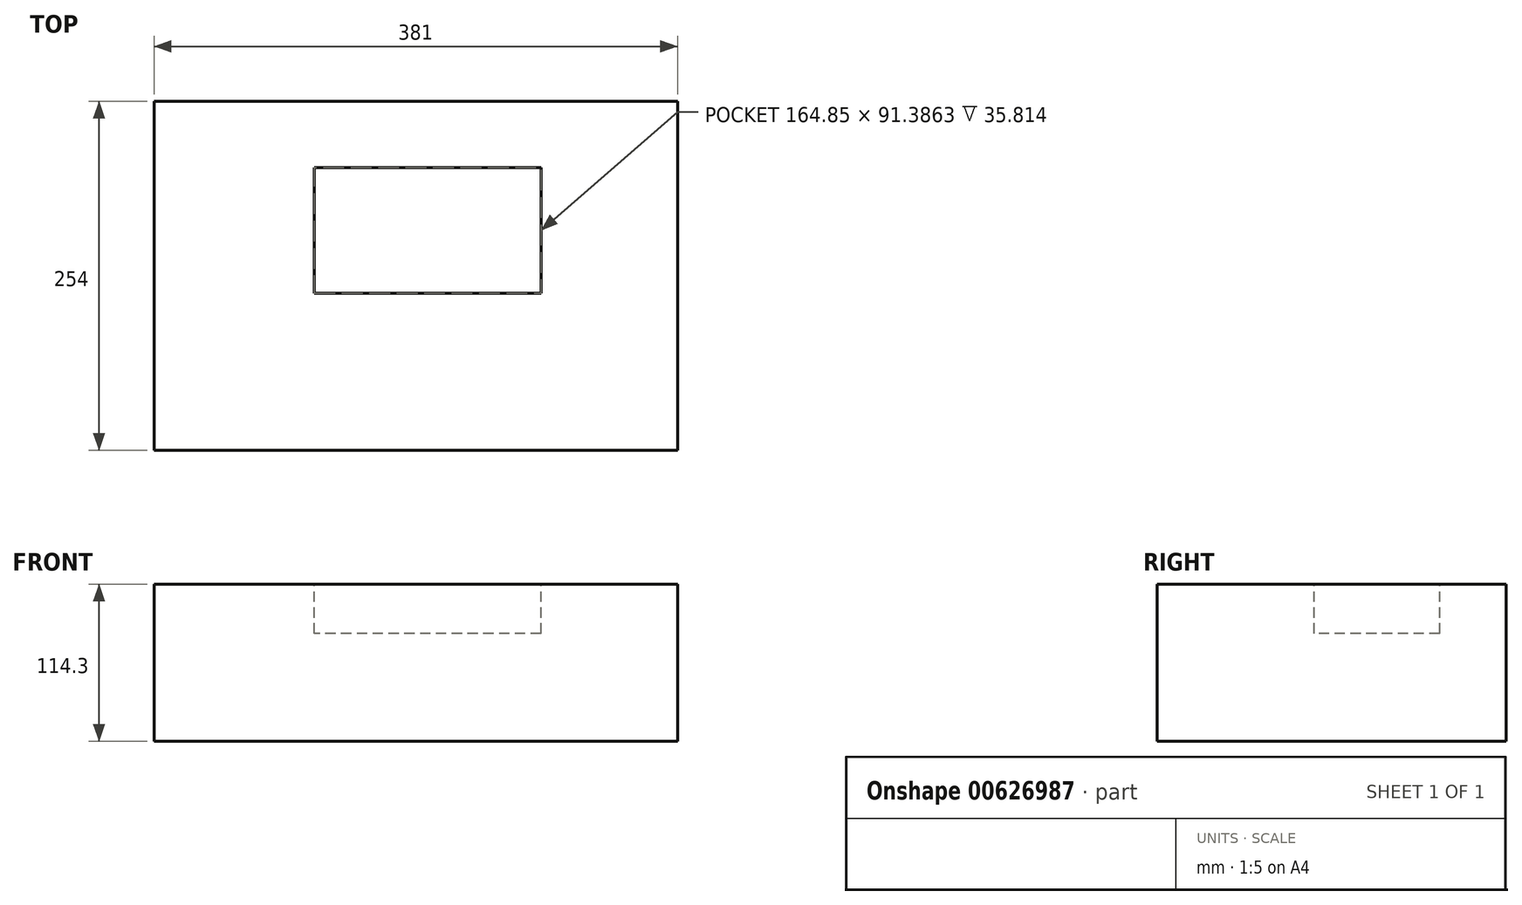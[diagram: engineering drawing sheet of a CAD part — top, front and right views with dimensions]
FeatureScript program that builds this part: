
annotation { "Feature Type Name" : "Feature", "Feature Type Description" : "" }
export const myFeature = defineFeature(function(context is Context, id is Id, definition is map)
    precondition{}
    {
        {
            var Q0;
            Q0=qCreatedBy(makeId("Top.planeOp"),FACE);
            var sketch = newSketch(context, id + "F0", { "sketchPlane" : qUnion([Q0])});
            skLineSegment(sketch, "E0.bottom", {"start": v(-157.42, 126.4) * mm, "end": v(223.58, 126.4) * mm});
            skLineSegment(sketch, "E0.top", {"start": v(-157.42, -127.6) * mm, "end": v(223.58, -127.6) * mm});
            skLineSegment(sketch, "E0.left", {"start": v(-157.42, 126.4) * mm, "end": v(-157.42, -127.6) * mm});
            skLineSegment(sketch, "E0.right", {"start": v(223.58, 126.4) * mm, "end": v(223.58, -127.6) * mm});
            skLineSegment(sketch, "E1", {"start": v(-157.42, 126.4) * mm, "end": v(223.58, -127.6) * mm});
            skLineSegment(sketch, "E2", {"start": v(-157.42, -121.17) * mm, "end": v(223.58, 126.4) * mm});
            skSolve(sketch);
        }
        {
            var Q0;
            Q0 = qSketchRegion(id + "F0", true);
            extrude(context, id + "F1", {"entities" : qUnion([Q0]), "depth" : 114.3 * mm, "offsetDistance" : 25.4 * mm});
        }
        {
            var Q0;
            Q0=makeQuery(id+"F1.opExtrude","CAP_FACE",FACE,{"disambiguationData":[OSD([sQuery(id+"F0.wireOp",EDGE,"E0.bottom"),sQuery(id+"F0.wireOp",EDGE,"E0.top"),sQuery(id+"F0.wireOp",EDGE,"E0.left"),sQuery(id+"F0.wireOp",EDGE,"E0.right")])],"isStart":false});
            var sketch = newSketch(context, id + "F2", { "sketchPlane" : qUnion([Q0])});
            skLineSegment(sketch, "E3.bottom", {"start": v(124.22, 78.08) * mm, "end": v(-40.63, 78.08) * mm});
            skLineSegment(sketch, "E3.top", {"start": v(124.22, -13.3) * mm, "end": v(-40.63, -13.3) * mm});
            skLineSegment(sketch, "E3.left", {"start": v(124.22, 78.08) * mm, "end": v(124.22, -13.3) * mm});
            skLineSegment(sketch, "E3.right", {"start": v(-40.63, 78.08) * mm, "end": v(-40.63, -13.3) * mm});
            skSolve(sketch);
        }
        {
            var Q0;
            Q0 = qSketchRegion(id + "F2", true);
            extrude(context, id + "F3", {"entities" : qUnion([Q0]), "operationType" : NewBodyOperationType.REMOVE, "oppositeDirection" : true, "depth" : 35.81 * mm, "offsetDistance" : 25.4 * mm});
        }
    });
